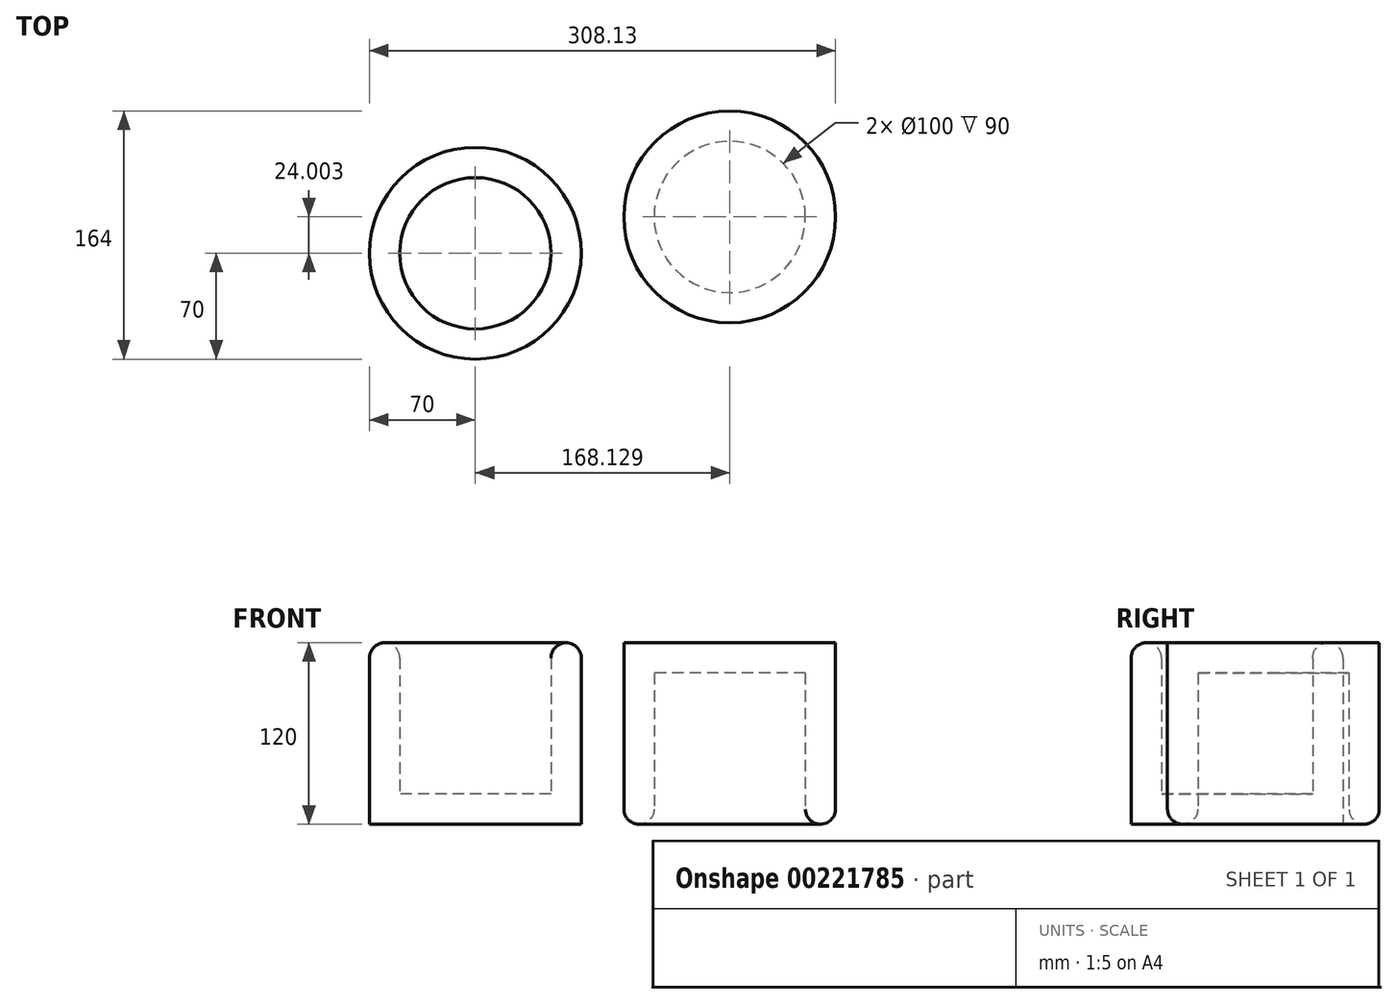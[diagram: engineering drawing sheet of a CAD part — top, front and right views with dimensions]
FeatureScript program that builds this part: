
annotation { "Feature Type Name" : "Feature", "Feature Type Description" : "" }
export const myFeature = defineFeature(function(context is Context, id is Id, definition is map)
    precondition{}
    {
        {
            assignVariable(context, id + "F0", {"name" : "insulation_thickness", "anyValue" : 20});
        }
        {
            assignVariable(context, id + "F1", {"name" : "cooler_depth", "anyValue" : 100});
        }
        {
            var Q0;
            Q0=qCreatedBy(makeId("Top.planeOp"),FACE);
            var sketch = newSketch(context, id + "F2", { "sketchPlane" : qUnion([Q0])});
            skCircle(sketch, "E0", {"center": v(0, 0) * mm, "radius": 70 * mm});
            skSolve(sketch);
        }
        {
            var Q0;
            Q0=makeQuery(id+"F2.imprint","IMPRINT",FACE,{"disambiguationData":[TD([[makeQuery(id+"F2.imprint","IMPRINT",EDGE,{"derivedFrom":sQuery(id+"F2.wireOp",EDGE,"E0")}),1.0]])]});
            extrude(context, id + "F3", {"entities" : qUnion([Q0]), "depth" : (getVariable(context, 'insulation_thickness')) * mm});
        }
        {
            var Q0;
            Q0=makeQuery(id+"F3.opExtrude","CAP_FACE",FACE,{"disambiguationData":[OSD([sQuery(id+"F2.wireOp",EDGE,"E0")])],"isStart":false});
            var sketch = newSketch(context, id + "F4", { "sketchPlane" : qUnion([Q0])});
            skCircle(sketch, "E1", {"center": v(0, 0) * mm, "radius": 50 * mm});
            skSolve(sketch);
        }
        {
            var Q0;
            Q0=makeQuery(id+"F4.imprint","IMPRINT",FACE,{"disambiguationData":[TD([[makeQuery(id+"F4.imprint","IMPRINT",EDGE,{"derivedFrom":sQuery(id+"F4.wireOp",EDGE,"E1")}),-1.0]])]});
            extrude(context, id + "F5", {"entities" : qUnion([Q0]), "operationType" : NewBodyOperationType.ADD, "depth" : (getVariable(context, 'cooler_depth')) * mm});
        }
        {
            var Q0;
            Q0=makeQuery(id+"F5.opExtrude","CAP_EDGE",EDGE,{"disambiguationData":[OSD([sQuery(id+"F4.wireOp",EDGE,"E1")])],"isStart":false});
            var Q1;
            Q1=makeQuery(id+"F5.opExtrude","CAP_EDGE",EDGE,{"disambiguationData":[OSD([sQuery(id+"F2.wireOp",EDGE,"E0")])],"isStart":false});
            fillet(context, id + "F6", {"entities" : qUnion([Q0, Q1]), "radius" : (getVariable(context, 'insulation_thickness') / 2) * mm, "tangentPropagation" : true, "allowEdgeOverflow" : false});
        }
        {
            var Q0;
            Q0=qCreatedBy(makeId("Top.planeOp"),FACE);
            var sketch = newSketch(context, id + "F7", { "sketchPlane" : qUnion([Q0])});
            skCircle(sketch, "E2", {"center": v(168.13, 24) * mm, "radius": 70 * mm});
            skCircle(sketch, "E3", {"center": v(168.13, 24) * mm, "radius": 50 * mm});
            skSolve(sketch);
        }
        {
            var Q0;
            Q0 = qSketchRegion(id + "F7", true);
            extrude(context, id + "F8", {"entities" : qUnion([Q0]), "depth" : (getVariable(context, 'cooler_depth') + getVariable(context, 'insulation_thickness')) * mm});
        }
        {
            var Q0;
            Q0=makeQuery(id+"F8.opExtrude","CAP_FACE",FACE,{"disambiguationData":[OSD([sQuery(id+"F7.wireOp",EDGE,"E2")])],"isStart":false});
            var sketch = newSketch(context, id + "F9", { "sketchPlane" : qUnion([Q0])});
            skCircle(sketch, "E4.0", {"center": v(168.13, 24) * mm, "radius": 50 * mm});
            skSolve(sketch);
        }
        {
            var Q0;
            Q0=makeQuery(id+"F8.opExtrude","CAP_EDGE",EDGE,{"disambiguationData":[OSD([sQuery(id+"F7.wireOp",EDGE,"E2")])],"isStart":true});
            var Q1;
            Q1=makeQuery(id+"F8.opExtrude","CAP_EDGE",EDGE,{"disambiguationData":[OSD([sQuery(id+"F7.wireOp",EDGE,"E3")])],"isStart":true});
            fillet(context, id + "F10", {"entities" : qUnion([Q0, Q1]), "radius" : 10 * mm, "tangentPropagation" : true, "allowEdgeOverflow" : false});
        }
        {
            var Q0;
            Q0=makeQuery(id+"F9.imprint","IMPRINT",FACE,{"disambiguationData":[TD([[makeQuery(id+"F9.imprint","IMPRINT",EDGE,{"derivedFrom":sQuery(id+"F9.wireOp",EDGE,"E4.0")}),1.0]])]});
            extrude(context, id + "F11", {"entities" : qUnion([Q0]), "operationType" : NewBodyOperationType.ADD, "oppositeDirection" : true, "depth" : (getVariable(context, 'insulation_thickness')) * mm});
        }
    });
